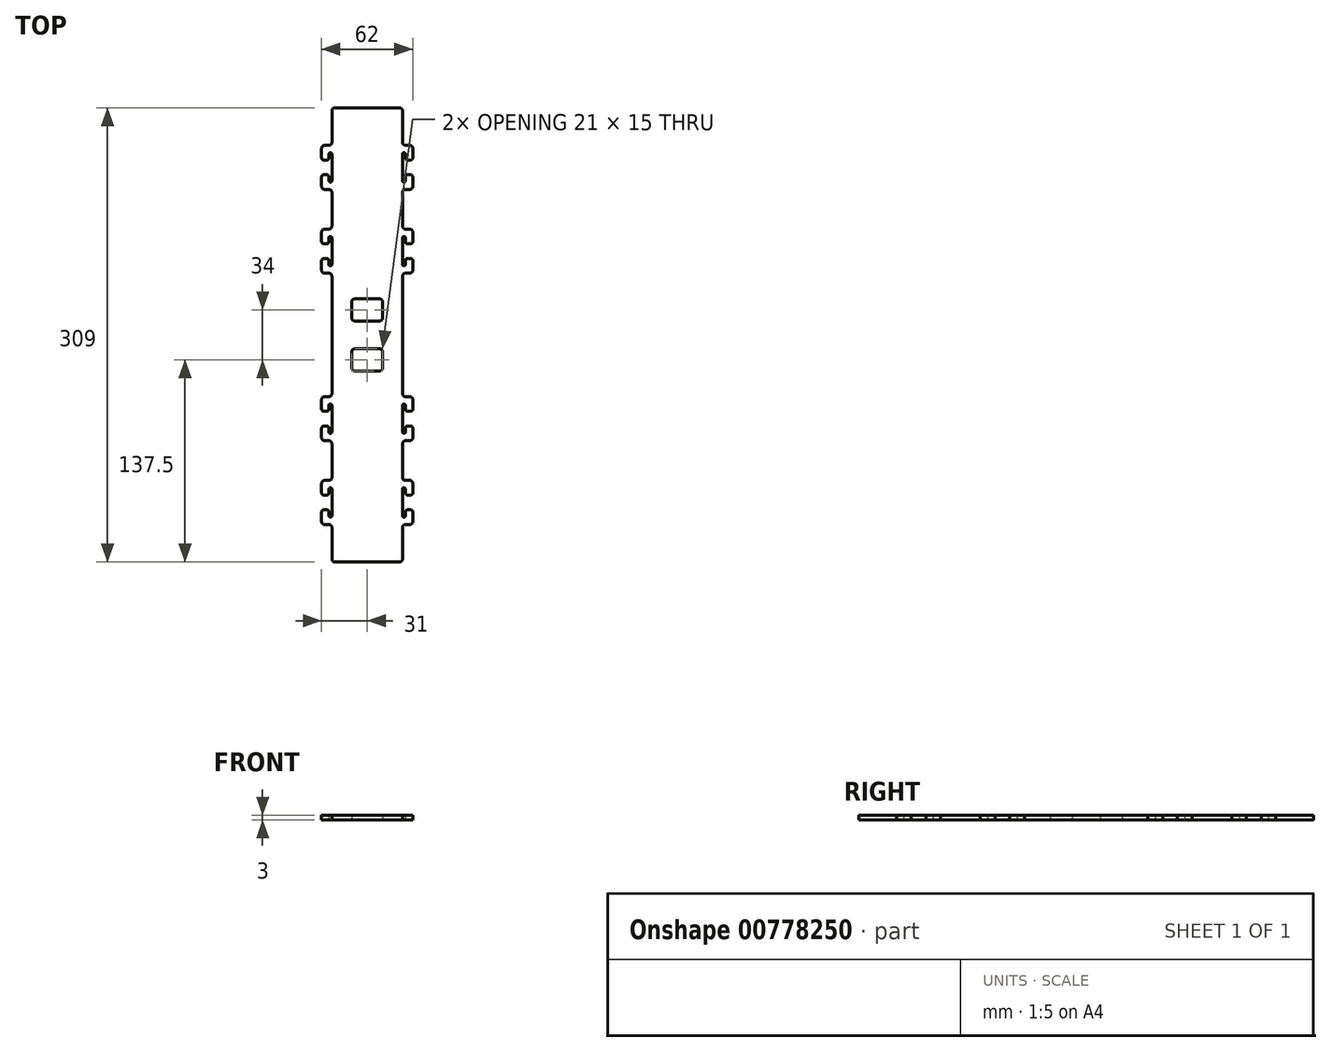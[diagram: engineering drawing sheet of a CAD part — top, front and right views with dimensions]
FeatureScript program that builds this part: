
annotation { "Feature Type Name" : "Feature", "Feature Type Description" : "" }
export const myFeature = defineFeature(function(context is Context, id is Id, definition is map)
    precondition{}
    {
        {
            var Q0;
            Q0=qCreatedBy(makeId("Top.planeOp"),FACE);
            var sketch = newSketch(context, id + "F0", { "sketchPlane" : qUnion([Q0])});
            skLineSegment(sketch, "E0.bottom", {"start": v(2, 0) * mm, "end": v(24, 0) * mm});
            skLineSegment(sketch, "E0.left", {"start": v(0, 2) * mm, "end": v(0, 23.5) * mm});
            skLineSegment(sketch, "E1", {"start": v(24, 154.5) * mm, "end": v(24, 0) * mm, "construction": true});
            skLineSegment(sketch, "E2.bottom", {"start": v(-5, 25.5) * mm, "end": v(-2, 25.5) * mm});
            skLineSegment(sketch, "E2.top", {"start": v(-5, 55.5) * mm, "end": v(-2, 55.5) * mm});
            skLineSegment(sketch, "E2.left", {"start": v(-7, 27.5) * mm, "end": v(-7, 34) * mm});
            skPoint(sketch, "E2.middle", {"position": v(24, 40.5) * mm});
            skLineSegment(sketch, "E3.bottom", {"start": v(-5, 82.5) * mm, "end": v(-2, 82.5) * mm});
            skLineSegment(sketch, "E3.top", {"start": v(-5, 112.5) * mm, "end": v(-2, 112.5) * mm});
            skLineSegment(sketch, "E3.left", {"start": v(-7, 84.5) * mm, "end": v(-7, 91) * mm});
            skPoint(sketch, "E3.middle", {"position": v(24, 97.5) * mm});
            skLineSegment(sketch, "E4", {"start": v(-7, 97.5) * mm, "end": v(24, 97.5) * mm, "construction": true});
            skLineSegment(sketch, "E5", {"start": v(-7, 40.5) * mm, "end": v(24, 40.5) * mm, "construction": true});
            skLineSegment(sketch, "E6", {"start": v(-1, 49.5) * mm, "end": v(-1, 31.5) * mm, "construction": true});
            skLineSegment(sketch, "E7", {"start": v(-1, 88.5) * mm, "end": v(-1, 106.5) * mm, "construction": true});
            skArc(sketch, "E8.0.startCap", {"start": v(0, 88.5) * mm, "mid": v(-1, 87.5) * mm, "end": v(-2, 88.5) * mm});
            skArc(sketch, "E8.0.endCap", {"start": v(-2, 106.5) * mm, "mid": v(-1, 107.5) * mm, "end": v(0, 106.5) * mm});
            skLineSegment(sketch, "E8.0.left", {"start": v(-2, 88.5) * mm, "end": v(-2, 91) * mm});
            skLineSegment(sketch, "E8.0.right", {"start": v(0, 88.5) * mm, "end": v(0, 106.5) * mm});
            skArc(sketch, "E8.1.startCap", {"start": v(-2, 49.5) * mm, "mid": v(-1, 50.5) * mm, "end": v(0, 49.5) * mm});
            skArc(sketch, "E8.1.endCap", {"start": v(0, 31.5) * mm, "mid": v(-1, 30.5) * mm, "end": v(-2, 31.5) * mm});
            skLineSegment(sketch, "E8.1.left", {"start": v(0, 49.5) * mm, "end": v(0, 31.5) * mm});
            skLineSegment(sketch, "E8.1.right", {"start": v(-2, 49.5) * mm, "end": v(-2, 47) * mm});
            skLineSegment(sketch, "E9", {"start": v(-5.5, 102.5) * mm, "end": v(-3.5, 102.5) * mm});
            skLineSegment(sketch, "E10", {"start": v(-5.5, 92.5) * mm, "end": v(-3.5, 92.5) * mm});
            skLineSegment(sketch, "E11", {"start": v(-5.5, 45.5) * mm, "end": v(-3.5, 45.5) * mm});
            skLineSegment(sketch, "E12", {"start": v(-5.5, 35.5) * mm, "end": v(-3.5, 35.5) * mm});
            skLineSegment(sketch, "E13.trimOffspring", {"start": v(-7, 47) * mm, "end": v(-7, 53.5) * mm});
            skLineSegment(sketch, "E14.trimOffspring", {"start": v(-2, 34) * mm, "end": v(-2, 31.5) * mm});
            skLineSegment(sketch, "E15.trimOffspring", {"start": v(-7, 104) * mm, "end": v(-7, 110.5) * mm});
            skLineSegment(sketch, "E16.trimOffspring", {"start": v(-2, 104) * mm, "end": v(-2, 106.5) * mm});
            skLineSegment(sketch, "E17", {"start": v(0, 112.5) * mm, "end": v(24, 112.5) * mm, "construction": true});
            skLineSegment(sketch, "E18", {"start": v(0, 114.5) * mm, "end": v(0, 154.5) * mm});
            skLineSegment(sketch, "E19", {"start": v(0, 82.5) * mm, "end": v(24, 82.5) * mm, "construction": true});
            skLineSegment(sketch, "E20", {"start": v(0, 82.5) * mm, "end": v(0, 112.5) * mm, "construction": true});
            skLineSegment(sketch, "E21", {"start": v(0, 57.5) * mm, "end": v(0, 80.5) * mm});
            skLineSegment(sketch, "E22", {"start": v(0, 55.5) * mm, "end": v(24, 55.5) * mm, "construction": true});
            skLineSegment(sketch, "E23", {"start": v(0, 25.5) * mm, "end": v(0, 55.5) * mm, "construction": true});
            skLineSegment(sketch, "E24", {"start": v(0, 25.5) * mm, "end": v(24, 25.5) * mm, "construction": true});
            skPoint(sketch, "E25.visualSharp", {"position": v(0, 0) * mm});
            skLineSegment(sketch, "E26.bottom", {"start": v(15.5, 130) * mm, "end": v(24, 130) * mm});
            skLineSegment(sketch, "E26.top", {"start": v(15.5, 145) * mm, "end": v(24, 145) * mm});
            skLineSegment(sketch, "E26.left", {"start": v(13.5, 132) * mm, "end": v(13.5, 143) * mm});
            skLineSegment(sketch, "E27", {"start": v(24, 137.5) * mm, "end": v(13.5, 137.5) * mm, "construction": true});
            skPoint(sketch, "E28.visualSharp", {"position": v(13.5, 145) * mm});
            skArc(sketch, "E28.filletArc", {"start": v(15.5, 145) * mm, "mid": v(14.09, 144.41) * mm, "end": v(13.5, 143) * mm});
            skPoint(sketch, "E29.visualSharp", {"position": v(13.5, 130) * mm});
            skArc(sketch, "E29.filletArc", {"start": v(13.5, 132) * mm, "mid": v(14.09, 130.59) * mm, "end": v(15.5, 130) * mm});
            skPoint(sketch, "E30.visualSharp", {"position": v(0, 112.5) * mm});
            skArc(sketch, "E30.filletArc", {"start": v(-2, 112.5) * mm, "mid": v(-0.59, 113.09) * mm, "end": v(0, 114.5) * mm});
            skPoint(sketch, "E31.visualSharp", {"position": v(-7, 112.5) * mm});
            skArc(sketch, "E31.filletArc", {"start": v(-5, 112.5) * mm, "mid": v(-6.41, 111.91) * mm, "end": v(-7, 110.5) * mm});
            skPoint(sketch, "E32.visualSharp", {"position": v(-7, 82.5) * mm});
            skArc(sketch, "E32.filletArc", {"start": v(-7, 84.5) * mm, "mid": v(-6.41, 83.09) * mm, "end": v(-5, 82.5) * mm});
            skPoint(sketch, "E33.visualSharp", {"position": v(0, 82.5) * mm});
            skArc(sketch, "E33.filletArc", {"start": v(0, 80.5) * mm, "mid": v(-0.59, 81.91) * mm, "end": v(-2, 82.5) * mm});
            skPoint(sketch, "E34.visualSharp", {"position": v(0, 55.5) * mm});
            skArc(sketch, "E34.filletArc", {"start": v(-2, 55.5) * mm, "mid": v(-0.59, 56.09) * mm, "end": v(0, 57.5) * mm});
            skPoint(sketch, "E35.visualSharp", {"position": v(-7, 55.5) * mm});
            skArc(sketch, "E35.filletArc", {"start": v(-5, 55.5) * mm, "mid": v(-6.41, 54.91) * mm, "end": v(-7, 53.5) * mm});
            skPoint(sketch, "E36.visualSharp", {"position": v(-7, 25.5) * mm});
            skArc(sketch, "E36.filletArc", {"start": v(-7, 27.5) * mm, "mid": v(-6.41, 26.09) * mm, "end": v(-5, 25.5) * mm});
            skPoint(sketch, "E37.visualSharp", {"position": v(0, 25.5) * mm});
            skArc(sketch, "E37.filletArc", {"start": v(0, 23.5) * mm, "mid": v(-0.59, 24.91) * mm, "end": v(-2, 25.5) * mm});
            skArc(sketch, "E38.filletArc", {"start": v(0, 2) * mm, "mid": v(0.59, 0.59) * mm, "end": v(2, 0) * mm});
            skPoint(sketch, "E39.visualSharp", {"position": v(-7, 102.5) * mm});
            skArc(sketch, "E39.filletArc", {"start": v(-7, 104) * mm, "mid": v(-6.56, 102.94) * mm, "end": v(-5.5, 102.5) * mm});
            skPoint(sketch, "E40.visualSharp", {"position": v(-2, 102.5) * mm});
            skArc(sketch, "E40.filletArc", {"start": v(-3.5, 102.5) * mm, "mid": v(-2.44, 102.94) * mm, "end": v(-2, 104) * mm});
            skPoint(sketch, "E41.visualSharp", {"position": v(-7, 92.5) * mm});
            skArc(sketch, "E41.filletArc", {"start": v(-5.5, 92.5) * mm, "mid": v(-6.56, 92.06) * mm, "end": v(-7, 91) * mm});
            skPoint(sketch, "E42.visualSharp", {"position": v(-2, 92.5) * mm});
            skArc(sketch, "E42.filletArc", {"start": v(-2, 91) * mm, "mid": v(-2.44, 92.06) * mm, "end": v(-3.5, 92.5) * mm});
            skPoint(sketch, "E43.visualSharp", {"position": v(-7, 45.5) * mm});
            skArc(sketch, "E43.filletArc", {"start": v(-7, 47) * mm, "mid": v(-6.56, 45.94) * mm, "end": v(-5.5, 45.5) * mm});
            skPoint(sketch, "E44.visualSharp", {"position": v(-2, 45.5) * mm});
            skArc(sketch, "E44.filletArc", {"start": v(-3.5, 45.5) * mm, "mid": v(-2.44, 45.94) * mm, "end": v(-2, 47) * mm});
            skPoint(sketch, "E45.visualSharp", {"position": v(-7, 35.5) * mm});
            skArc(sketch, "E45.filletArc", {"start": v(-5.5, 35.5) * mm, "mid": v(-6.56, 35.06) * mm, "end": v(-7, 34) * mm});
            skPoint(sketch, "E46.visualSharp", {"position": v(-2, 35.5) * mm});
            skArc(sketch, "E46.filletArc", {"start": v(-2, 34) * mm, "mid": v(-2.44, 35.06) * mm, "end": v(-3.5, 35.5) * mm});
            skLineSegment(sketch, "E47.MirrorCS", {"start": v(48, 114.5) * mm, "end": v(48, 154.5) * mm});
            skArc(sketch, "E48.MirrorCS", {"start": v(50, 112.5) * mm, "mid": v(48.59, 113.09) * mm, "end": v(48, 114.5) * mm});
            skLineSegment(sketch, "E49.MirrorCS", {"start": v(53, 112.5) * mm, "end": v(50, 112.5) * mm});
            skArc(sketch, "E50.MirrorCS", {"start": v(53, 112.5) * mm, "mid": v(54.41, 111.91) * mm, "end": v(55, 110.5) * mm});
            skLineSegment(sketch, "E51.MirrorCS", {"start": v(55, 104) * mm, "end": v(55, 110.5) * mm});
            skArc(sketch, "E52.MirrorCS", {"start": v(55, 104) * mm, "mid": v(54.56, 102.94) * mm, "end": v(53.5, 102.5) * mm});
            skLineSegment(sketch, "E53.MirrorCS", {"start": v(53.5, 102.5) * mm, "end": v(51.5, 102.5) * mm});
            skArc(sketch, "E54.MirrorCS", {"start": v(51.5, 102.5) * mm, "mid": v(50.44, 102.94) * mm, "end": v(50, 104) * mm});
            skLineSegment(sketch, "E55.MirrorCS", {"start": v(50, 104) * mm, "end": v(50, 106.5) * mm});
            skArc(sketch, "E56.MirrorCS", {"start": v(50, 106.5) * mm, "mid": v(49, 107.5) * mm, "end": v(48, 106.5) * mm});
            skArc(sketch, "E57.MirrorCS", {"start": v(48, 88.5) * mm, "mid": v(49, 87.5) * mm, "end": v(50, 88.5) * mm});
            skLineSegment(sketch, "E58.MirrorCS", {"start": v(50, 88.5) * mm, "end": v(50, 91) * mm});
            skArc(sketch, "E59.MirrorCS", {"start": v(50, 91) * mm, "mid": v(50.44, 92.06) * mm, "end": v(51.5, 92.5) * mm});
            skLineSegment(sketch, "E60.MirrorCS", {"start": v(53.5, 92.5) * mm, "end": v(51.5, 92.5) * mm});
            skArc(sketch, "E61.MirrorCS", {"start": v(53.5, 92.5) * mm, "mid": v(54.56, 92.06) * mm, "end": v(55, 91) * mm});
            skLineSegment(sketch, "E62.MirrorCS", {"start": v(55, 84.5) * mm, "end": v(55, 91) * mm});
            skArc(sketch, "E63.MirrorCS", {"start": v(55, 84.5) * mm, "mid": v(54.41, 83.09) * mm, "end": v(53, 82.5) * mm});
            skLineSegment(sketch, "E64.MirrorCS", {"start": v(53, 82.5) * mm, "end": v(50, 82.5) * mm});
            skArc(sketch, "E65.MirrorCS", {"start": v(48, 80.5) * mm, "mid": v(48.59, 81.91) * mm, "end": v(50, 82.5) * mm});
            skLineSegment(sketch, "E66.MirrorCS", {"start": v(48, 57.5) * mm, "end": v(48, 80.5) * mm});
            skArc(sketch, "E67.MirrorCS", {"start": v(50, 55.5) * mm, "mid": v(48.59, 56.09) * mm, "end": v(48, 57.5) * mm});
            skLineSegment(sketch, "E68.MirrorCS", {"start": v(53, 55.5) * mm, "end": v(50, 55.5) * mm});
            skArc(sketch, "E69.MirrorCS", {"start": v(53, 55.5) * mm, "mid": v(54.41, 54.91) * mm, "end": v(55, 53.5) * mm});
            skLineSegment(sketch, "E70.MirrorCS", {"start": v(55, 47) * mm, "end": v(55, 53.5) * mm});
            skArc(sketch, "E71.MirrorCS", {"start": v(55, 47) * mm, "mid": v(54.56, 45.94) * mm, "end": v(53.5, 45.5) * mm});
            skLineSegment(sketch, "E72.MirrorCS", {"start": v(53.5, 45.5) * mm, "end": v(51.5, 45.5) * mm});
            skPoint(sketch, "E73.MirrorP", {"position": v(50, 45.5) * mm});
            skLineSegment(sketch, "E74.MirrorCS", {"start": v(50, 49.5) * mm, "end": v(50, 47) * mm});
            skArc(sketch, "E75.MirrorCS", {"start": v(50, 49.5) * mm, "mid": v(49, 50.5) * mm, "end": v(48, 49.5) * mm});
            skArc(sketch, "E76.MirrorCS", {"start": v(51.5, 45.5) * mm, "mid": v(50.44, 45.94) * mm, "end": v(50, 47) * mm});
            skArc(sketch, "E77.MirrorCS", {"start": v(48, 31.5) * mm, "mid": v(49, 30.5) * mm, "end": v(50, 31.5) * mm});
            skLineSegment(sketch, "E78.MirrorCS", {"start": v(50, 34) * mm, "end": v(50, 31.5) * mm});
            skArc(sketch, "E79.MirrorCS", {"start": v(50, 34) * mm, "mid": v(50.44, 35.06) * mm, "end": v(51.5, 35.5) * mm});
            skLineSegment(sketch, "E80.MirrorCS", {"start": v(53.5, 35.5) * mm, "end": v(51.5, 35.5) * mm});
            skArc(sketch, "E81.MirrorCS", {"start": v(53.5, 35.5) * mm, "mid": v(54.56, 35.06) * mm, "end": v(55, 34) * mm});
            skLineSegment(sketch, "E82.MirrorCS", {"start": v(55, 27.5) * mm, "end": v(55, 34) * mm});
            skArc(sketch, "E83.MirrorCS", {"start": v(55, 27.5) * mm, "mid": v(54.41, 26.09) * mm, "end": v(53, 25.5) * mm});
            skLineSegment(sketch, "E84.MirrorCS", {"start": v(53, 25.5) * mm, "end": v(50, 25.5) * mm});
            skArc(sketch, "E85.MirrorCS", {"start": v(48, 23.5) * mm, "mid": v(48.59, 24.91) * mm, "end": v(50, 25.5) * mm});
            skLineSegment(sketch, "E86.MirrorCS", {"start": v(48, 2) * mm, "end": v(48, 23.5) * mm});
            skArc(sketch, "E87.MirrorCS", {"start": v(48, 2) * mm, "mid": v(47.41, 0.59) * mm, "end": v(46, 0) * mm});
            skLineSegment(sketch, "E88.MirrorCS", {"start": v(46, 0) * mm, "end": v(24, 0) * mm});
            skLineSegment(sketch, "E89", {"start": v(48, 106.5) * mm, "end": v(48, 88.5) * mm});
            skLineSegment(sketch, "E90", {"start": v(48, 49.5) * mm, "end": v(48, 31.5) * mm});
            skLineSegment(sketch, "E91.MirrorCS", {"start": v(32.5, 145) * mm, "end": v(24, 145) * mm});
            skArc(sketch, "E92.MirrorCS", {"start": v(32.5, 145) * mm, "mid": v(33.91, 144.41) * mm, "end": v(34.5, 143) * mm});
            skLineSegment(sketch, "E93.MirrorCS", {"start": v(34.5, 132) * mm, "end": v(34.5, 143) * mm});
            skArc(sketch, "E94.MirrorCS", {"start": v(34.5, 132) * mm, "mid": v(33.91, 130.59) * mm, "end": v(32.5, 130) * mm});
            skLineSegment(sketch, "E95.MirrorCS", {"start": v(32.5, 130) * mm, "end": v(24, 130) * mm});
            skLineSegment(sketch, "E96", {"start": v(0, 154.5) * mm, "end": v(48, 154.5) * mm, "construction": true});
            skLineSegment(sketch, "E97.MirrorCS", {"start": v(0, 194.5) * mm, "end": v(0, 154.5) * mm});
            skArc(sketch, "E98.MirrorCS", {"start": v(-2, 196.5) * mm, "mid": v(-0.59, 195.91) * mm, "end": v(0, 194.5) * mm});
            skLineSegment(sketch, "E99.MirrorCS", {"start": v(-5, 196.5) * mm, "end": v(-2, 196.5) * mm});
            skArc(sketch, "E100.MirrorCS", {"start": v(-5, 196.5) * mm, "mid": v(-6.41, 197.09) * mm, "end": v(-7, 198.5) * mm});
            skLineSegment(sketch, "E101.MirrorCS", {"start": v(-7, 205) * mm, "end": v(-7, 198.5) * mm});
            skArc(sketch, "E102.MirrorCS", {"start": v(-7, 205) * mm, "mid": v(-6.56, 206.06) * mm, "end": v(-5.5, 206.5) * mm});
            skLineSegment(sketch, "E103.MirrorCS", {"start": v(-5.5, 206.5) * mm, "end": v(-3.5, 206.5) * mm});
            skArc(sketch, "E104.MirrorCS", {"start": v(-3.5, 206.5) * mm, "mid": v(-2.44, 206.06) * mm, "end": v(-2, 205) * mm});
            skLineSegment(sketch, "E105.MirrorCS", {"start": v(-2, 205) * mm, "end": v(-2, 202.5) * mm});
            skArc(sketch, "E106.MirrorCS", {"start": v(-2, 202.5) * mm, "mid": v(-1, 201.5) * mm, "end": v(0, 202.5) * mm});
            skArc(sketch, "E107.MirrorCS", {"start": v(0, 220.5) * mm, "mid": v(-1, 221.5) * mm, "end": v(-2, 220.5) * mm});
            skLineSegment(sketch, "E108.MirrorCS", {"start": v(-2, 220.5) * mm, "end": v(-2, 218) * mm});
            skArc(sketch, "E109.MirrorCS", {"start": v(-2, 218) * mm, "mid": v(-2.44, 216.94) * mm, "end": v(-3.5, 216.5) * mm});
            skLineSegment(sketch, "E110.MirrorCS", {"start": v(-5.5, 216.5) * mm, "end": v(-3.5, 216.5) * mm});
            skArc(sketch, "E111.MirrorCS", {"start": v(-5.5, 216.5) * mm, "mid": v(-6.56, 216.94) * mm, "end": v(-7, 218) * mm});
            skLineSegment(sketch, "E112.MirrorCS", {"start": v(-7, 224.5) * mm, "end": v(-7, 218) * mm});
            skArc(sketch, "E113.MirrorCS", {"start": v(-7, 224.5) * mm, "mid": v(-6.41, 225.91) * mm, "end": v(-5, 226.5) * mm});
            skLineSegment(sketch, "E114.MirrorCS", {"start": v(-5, 226.5) * mm, "end": v(-2, 226.5) * mm});
            skArc(sketch, "E115.MirrorCS", {"start": v(0, 228.5) * mm, "mid": v(-0.59, 227.09) * mm, "end": v(-2, 226.5) * mm});
            skLineSegment(sketch, "E116.MirrorCS", {"start": v(0, 251.5) * mm, "end": v(0, 228.5) * mm});
            skArc(sketch, "E117.MirrorCS", {"start": v(-2, 253.5) * mm, "mid": v(-0.59, 252.91) * mm, "end": v(0, 251.5) * mm});
            skLineSegment(sketch, "E118.MirrorCS", {"start": v(-5, 253.5) * mm, "end": v(-2, 253.5) * mm});
            skArc(sketch, "E119.MirrorCS", {"start": v(-5, 253.5) * mm, "mid": v(-6.41, 254.09) * mm, "end": v(-7, 255.5) * mm});
            skLineSegment(sketch, "E120.MirrorCS", {"start": v(-7, 262) * mm, "end": v(-7, 255.5) * mm});
            skArc(sketch, "E121.MirrorCS", {"start": v(-7, 262) * mm, "mid": v(-6.56, 263.06) * mm, "end": v(-5.5, 263.5) * mm});
            skLineSegment(sketch, "E122.MirrorCS", {"start": v(-5.5, 263.5) * mm, "end": v(-3.5, 263.5) * mm});
            skArc(sketch, "E123.MirrorCS", {"start": v(-3.5, 263.5) * mm, "mid": v(-2.44, 263.06) * mm, "end": v(-2, 262) * mm});
            skLineSegment(sketch, "E124.MirrorCS", {"start": v(-2, 259.5) * mm, "end": v(-2, 262) * mm});
            skArc(sketch, "E125.MirrorCS", {"start": v(-2, 259.5) * mm, "mid": v(-1, 258.5) * mm, "end": v(0, 259.5) * mm});
            skArc(sketch, "E126.MirrorCS", {"start": v(0, 277.5) * mm, "mid": v(-1, 278.5) * mm, "end": v(-2, 277.5) * mm});
            skLineSegment(sketch, "E127.MirrorCS", {"start": v(-2, 275) * mm, "end": v(-2, 277.5) * mm});
            skArc(sketch, "E128.MirrorCS", {"start": v(-2, 275) * mm, "mid": v(-2.44, 273.94) * mm, "end": v(-3.5, 273.5) * mm});
            skLineSegment(sketch, "E129.MirrorCS", {"start": v(-5.5, 273.5) * mm, "end": v(-3.5, 273.5) * mm});
            skArc(sketch, "E130.MirrorCS", {"start": v(-5.5, 273.5) * mm, "mid": v(-6.56, 273.94) * mm, "end": v(-7, 275) * mm});
            skLineSegment(sketch, "E131.MirrorCS", {"start": v(-7, 281.5) * mm, "end": v(-7, 275) * mm});
            skArc(sketch, "E132.MirrorCS", {"start": v(-7, 281.5) * mm, "mid": v(-6.41, 282.91) * mm, "end": v(-5, 283.5) * mm});
            skLineSegment(sketch, "E133.MirrorCS", {"start": v(-5, 283.5) * mm, "end": v(-2, 283.5) * mm});
            skArc(sketch, "E134.MirrorCS", {"start": v(0, 285.5) * mm, "mid": v(-0.59, 284.09) * mm, "end": v(-2, 283.5) * mm});
            skLineSegment(sketch, "E135.MirrorCS", {"start": v(0, 307) * mm, "end": v(0, 285.5) * mm});
            skArc(sketch, "E136.MirrorCS", {"start": v(0, 307) * mm, "mid": v(0.59, 308.41) * mm, "end": v(2, 309) * mm});
            skLineSegment(sketch, "E137.MirrorCS", {"start": v(2, 309) * mm, "end": v(24, 309) * mm});
            skLineSegment(sketch, "E138.MirrorCS", {"start": v(48, 194.5) * mm, "end": v(48, 154.5) * mm});
            skArc(sketch, "E139.MirrorCS", {"start": v(50, 196.5) * mm, "mid": v(48.59, 195.91) * mm, "end": v(48, 194.5) * mm});
            skLineSegment(sketch, "E140.MirrorCS", {"start": v(53, 196.5) * mm, "end": v(50, 196.5) * mm});
            skArc(sketch, "E141.MirrorCS", {"start": v(53, 196.5) * mm, "mid": v(54.41, 197.09) * mm, "end": v(55, 198.5) * mm});
            skLineSegment(sketch, "E142.MirrorCS", {"start": v(55, 205) * mm, "end": v(55, 198.5) * mm});
            skArc(sketch, "E143.MirrorCS", {"start": v(55, 205) * mm, "mid": v(54.56, 206.06) * mm, "end": v(53.5, 206.5) * mm});
            skLineSegment(sketch, "E144.MirrorCS", {"start": v(53.5, 206.5) * mm, "end": v(51.5, 206.5) * mm});
            skArc(sketch, "E145.MirrorCS", {"start": v(51.5, 206.5) * mm, "mid": v(50.44, 206.06) * mm, "end": v(50, 205) * mm});
            skLineSegment(sketch, "E146.MirrorCS", {"start": v(50, 205) * mm, "end": v(50, 202.5) * mm});
            skArc(sketch, "E147.MirrorCS", {"start": v(50, 202.5) * mm, "mid": v(49, 201.5) * mm, "end": v(48, 202.5) * mm});
            skLineSegment(sketch, "E148.MirrorCS", {"start": v(48, 202.5) * mm, "end": v(48, 220.5) * mm});
            skArc(sketch, "E149.MirrorCS", {"start": v(48, 220.5) * mm, "mid": v(49, 221.5) * mm, "end": v(50, 220.5) * mm});
            skLineSegment(sketch, "E150.MirrorCS", {"start": v(50, 220.5) * mm, "end": v(50, 218) * mm});
            skArc(sketch, "E151.MirrorCS", {"start": v(50, 218) * mm, "mid": v(50.44, 216.94) * mm, "end": v(51.5, 216.5) * mm});
            skLineSegment(sketch, "E152.MirrorCS", {"start": v(53.5, 216.5) * mm, "end": v(51.5, 216.5) * mm});
            skArc(sketch, "E153.MirrorCS", {"start": v(53.5, 216.5) * mm, "mid": v(54.56, 216.94) * mm, "end": v(55, 218) * mm});
            skLineSegment(sketch, "E154.MirrorCS", {"start": v(55, 224.5) * mm, "end": v(55, 218) * mm});
            skArc(sketch, "E155.MirrorCS", {"start": v(55, 224.5) * mm, "mid": v(54.41, 225.91) * mm, "end": v(53, 226.5) * mm});
            skLineSegment(sketch, "E156.MirrorCS", {"start": v(53, 226.5) * mm, "end": v(50, 226.5) * mm});
            skArc(sketch, "E157.MirrorCS", {"start": v(48, 228.5) * mm, "mid": v(48.59, 227.09) * mm, "end": v(50, 226.5) * mm});
            skLineSegment(sketch, "E158.MirrorCS", {"start": v(48, 251.5) * mm, "end": v(48, 228.5) * mm});
            skArc(sketch, "E159.MirrorCS", {"start": v(50, 253.5) * mm, "mid": v(48.59, 252.91) * mm, "end": v(48, 251.5) * mm});
            skLineSegment(sketch, "E160.MirrorCS", {"start": v(53, 253.5) * mm, "end": v(50, 253.5) * mm});
            skArc(sketch, "E161.MirrorCS", {"start": v(53, 253.5) * mm, "mid": v(54.41, 254.09) * mm, "end": v(55, 255.5) * mm});
            skLineSegment(sketch, "E162.MirrorCS", {"start": v(55, 262) * mm, "end": v(55, 255.5) * mm});
            skArc(sketch, "E163.MirrorCS", {"start": v(55, 262) * mm, "mid": v(54.56, 263.06) * mm, "end": v(53.5, 263.5) * mm});
            skLineSegment(sketch, "E164.MirrorCS", {"start": v(53.5, 263.5) * mm, "end": v(51.5, 263.5) * mm});
            skArc(sketch, "E165.MirrorCS", {"start": v(51.5, 263.5) * mm, "mid": v(50.44, 263.06) * mm, "end": v(50, 262) * mm});
            skLineSegment(sketch, "E166.MirrorCS", {"start": v(50, 259.5) * mm, "end": v(50, 262) * mm});
            skArc(sketch, "E167.MirrorCS", {"start": v(50, 259.5) * mm, "mid": v(49, 258.5) * mm, "end": v(48, 259.5) * mm});
            skLineSegment(sketch, "E168.MirrorCS", {"start": v(48, 259.5) * mm, "end": v(48, 277.5) * mm});
            skArc(sketch, "E169.MirrorCS", {"start": v(48, 277.5) * mm, "mid": v(49, 278.5) * mm, "end": v(50, 277.5) * mm});
            skLineSegment(sketch, "E170.MirrorCS", {"start": v(50, 275) * mm, "end": v(50, 277.5) * mm});
            skArc(sketch, "E171.MirrorCS", {"start": v(50, 275) * mm, "mid": v(50.44, 273.94) * mm, "end": v(51.5, 273.5) * mm});
            skLineSegment(sketch, "E172.MirrorCS", {"start": v(53.5, 273.5) * mm, "end": v(51.5, 273.5) * mm});
            skArc(sketch, "E173.MirrorCS", {"start": v(53.5, 273.5) * mm, "mid": v(54.56, 273.94) * mm, "end": v(55, 275) * mm});
            skLineSegment(sketch, "E174.MirrorCS", {"start": v(55, 281.5) * mm, "end": v(55, 275) * mm});
            skArc(sketch, "E175.MirrorCS", {"start": v(55, 281.5) * mm, "mid": v(54.41, 282.91) * mm, "end": v(53, 283.5) * mm});
            skLineSegment(sketch, "E176.MirrorCS", {"start": v(53, 283.5) * mm, "end": v(50, 283.5) * mm});
            skArc(sketch, "E177.MirrorCS", {"start": v(48, 285.5) * mm, "mid": v(48.59, 284.09) * mm, "end": v(50, 283.5) * mm});
            skLineSegment(sketch, "E178.MirrorCS", {"start": v(48, 307) * mm, "end": v(48, 285.5) * mm});
            skArc(sketch, "E179.MirrorCS", {"start": v(48, 307) * mm, "mid": v(47.41, 308.41) * mm, "end": v(46, 309) * mm});
            skLineSegment(sketch, "E180.MirrorCS", {"start": v(46, 309) * mm, "end": v(24, 309) * mm});
            skLineSegment(sketch, "E181.MirrorCS", {"start": v(15.5, 164) * mm, "end": v(24, 164) * mm});
            skArc(sketch, "E182.MirrorCS", {"start": v(15.5, 164) * mm, "mid": v(14.09, 164.59) * mm, "end": v(13.5, 166) * mm});
            skLineSegment(sketch, "E183.MirrorCS", {"start": v(13.5, 177) * mm, "end": v(13.5, 166) * mm});
            skArc(sketch, "E184.MirrorCS", {"start": v(13.5, 177) * mm, "mid": v(14.09, 178.41) * mm, "end": v(15.5, 179) * mm});
            skLineSegment(sketch, "E185.MirrorCS", {"start": v(15.5, 179) * mm, "end": v(24, 179) * mm});
            skLineSegment(sketch, "E186.MirrorCS", {"start": v(32.5, 179) * mm, "end": v(24, 179) * mm});
            skArc(sketch, "E187.MirrorCS", {"start": v(34.5, 177) * mm, "mid": v(33.91, 178.41) * mm, "end": v(32.5, 179) * mm});
            skLineSegment(sketch, "E188.MirrorCS", {"start": v(34.5, 177) * mm, "end": v(34.5, 166) * mm});
            skArc(sketch, "E189.MirrorCS", {"start": v(32.5, 164) * mm, "mid": v(33.91, 164.59) * mm, "end": v(34.5, 166) * mm});
            skLineSegment(sketch, "E190.MirrorCS", {"start": v(32.5, 164) * mm, "end": v(24, 164) * mm});
            skLineSegment(sketch, "E191", {"start": v(0, 277.5) * mm, "end": v(0, 259.5) * mm});
            skLineSegment(sketch, "E192", {"start": v(0, 220.5) * mm, "end": v(0, 202.5) * mm});
            skSolve(sketch);
        }
        {
            var Q0;
            Q0=makeQuery(id+"F0.imprint","IMPRINT",FACE,{"disambiguationData":[TD([[makeQuery(id+"F0.imprint","IMPRINT",EDGE,{"derivedFrom":sQuery(id+"F0.wireOp",EDGE,"E0.bottom")}),1.0]])]});
            extrude(context, id + "F1", {"entities" : qUnion([Q0]), "depth" : 3 * mm, "offsetDistance" : 25 * mm});
        }
    });
